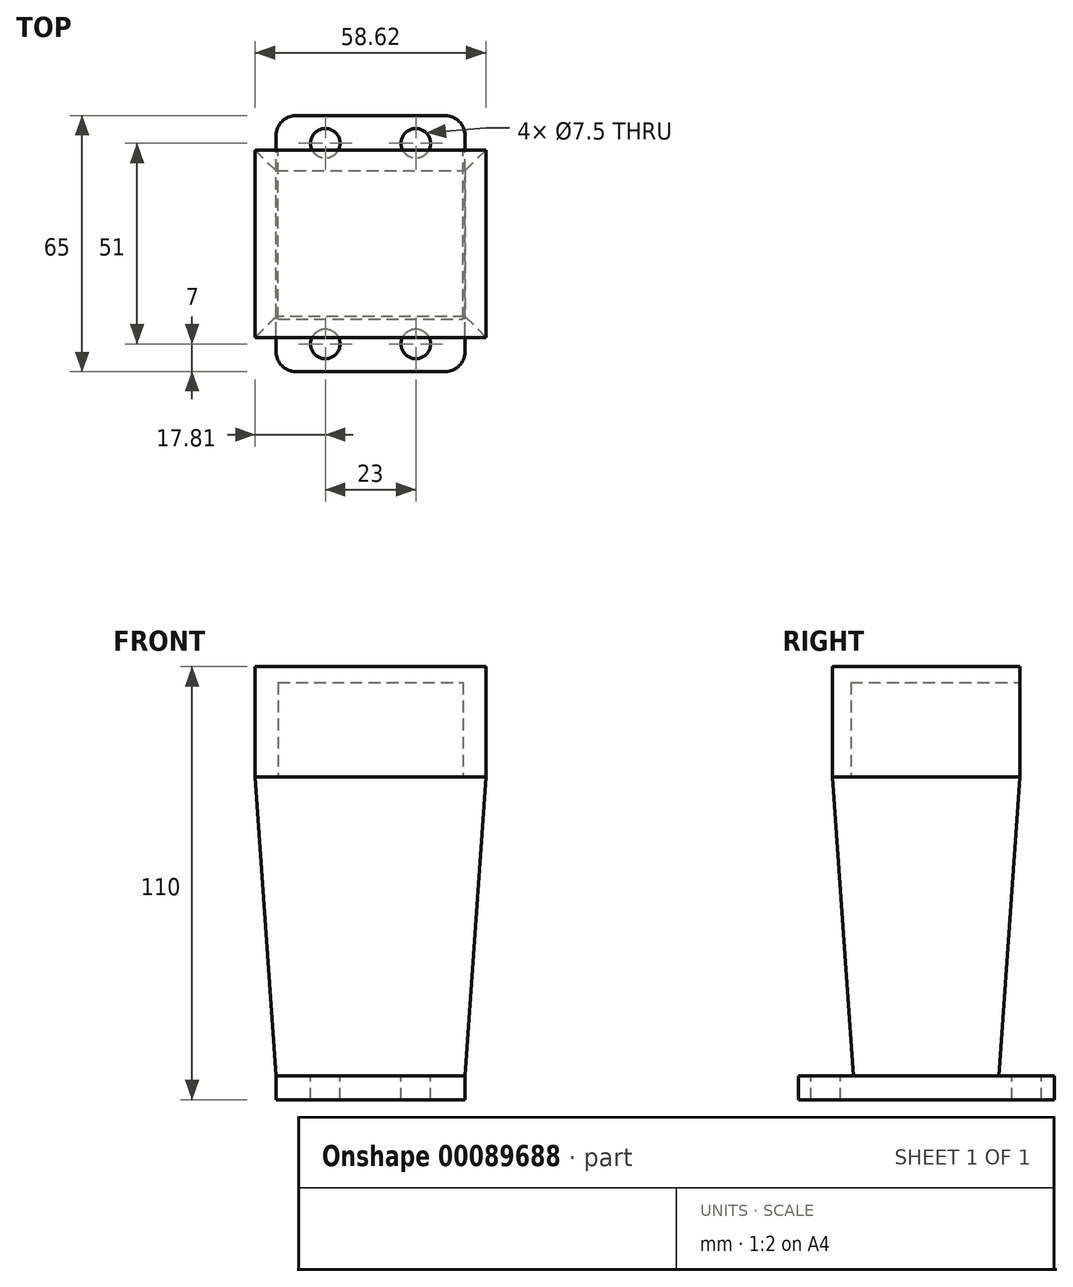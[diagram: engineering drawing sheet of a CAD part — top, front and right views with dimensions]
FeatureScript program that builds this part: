
annotation { "Feature Type Name" : "Feature", "Feature Type Description" : "" }
export const myFeature = defineFeature(function(context is Context, id is Id, definition is map)
    precondition{}
    {
        {
            var Q0;
            Q0=qCreatedBy(makeId("Top.planeOp"),FACE);
            var sketch = newSketch(context, id + "F0", { "sketchPlane" : qUnion([Q0])});
            skLineSegment(sketch, "E0.bottom", {"start": v(0, 0) * mm, "end": v(-48, 0) * mm});
            skLineSegment(sketch, "E0.top", {"start": v(0, 65) * mm, "end": v(-48, 65) * mm});
            skLineSegment(sketch, "E0.left", {"start": v(0, 0) * mm, "end": v(0, 65) * mm});
            skLineSegment(sketch, "E0.right", {"start": v(-48, 0) * mm, "end": v(-48, 65) * mm});
            skSolve(sketch);
        }
        {
            var Q0;
            Q0=makeQuery(id+"F0.imprint","IMPRINT",FACE,{"disambiguationData":[TD([[makeQuery(id+"F0.imprint","IMPRINT",EDGE,{"derivedFrom":sQuery(id+"F0.wireOp",EDGE,"E0.bottom")}),-1.0]])]});
            extrude(context, id + "F1", {"entities" : qUnion([Q0]), "depth" : 6 * mm});
        }
        {
            var Q0;
            Q0=makeQuery(id+"F1.opExtrude","CAP_FACE",FACE,{"disambiguationData":[OSD([sQuery(id+"F0.wireOp",EDGE,"E0.bottom"),sQuery(id+"F0.wireOp",EDGE,"E0.top"),sQuery(id+"F0.wireOp",EDGE,"E0.left"),sQuery(id+"F0.wireOp",EDGE,"E0.right")])],"isStart":false});
            var sketch = newSketch(context, id + "F2", { "sketchPlane" : qUnion([Q0])});
            skLineSegment(sketch, "E1", {"start": v(-24, 65) * mm, "end": v(-24, 0) * mm});
            skLineSegment(sketch, "E2", {"start": v(-48, 32.5) * mm, "end": v(0, 32.5) * mm});
            skLineSegment(sketch, "E3.bottom", {"start": v(0, 14) * mm, "end": v(-48, 14) * mm});
            skLineSegment(sketch, "E3.top", {"start": v(0, 51) * mm, "end": v(-48, 51) * mm});
            skLineSegment(sketch, "E3.left", {"start": v(0, 14) * mm, "end": v(0, 51) * mm});
            skLineSegment(sketch, "E3.right", {"start": v(-48, 14) * mm, "end": v(-48, 51) * mm});
            skPoint(sketch, "E3.middle", {"position": v(-24, 32.5) * mm});
            skSolve(sketch);
        }
        {
            var Q0;
            {var subQ0=sQuery(id+"F2.wireOp",EDGE,"E3.top");var subQ1=sQuery(id+"F2.wireOp",EDGE,"E1");var subQ2=makeQuery(id+"F2.imprint","INTERSECT",VERTEX,{"derivedFrom":[subQ1,subQ0]});Q0=makeQuery(id+"F2.imprint","IMPRINT",FACE,{"disambiguationData":[TD([[makeQuery(id+"F2.imprint","IMPRINT",EDGE,{"disambiguationData":[TD([[subQ2,-1.0]])],"derivedFrom":subQ1}),1.0]])]});}
            var Q1;
            {var subQ0=sQuery(id+"F2.wireOp",EDGE,"E3.top");var subQ1=sQuery(id+"F2.wireOp",EDGE,"E1");var subQ2=makeQuery(id+"F2.imprint","INTERSECT",VERTEX,{"derivedFrom":[subQ1,subQ0]});Q1=makeQuery(id+"F2.imprint","IMPRINT",FACE,{"disambiguationData":[TD([[makeQuery(id+"F2.imprint","IMPRINT",EDGE,{"disambiguationData":[TD([[subQ2,-1.0]])],"derivedFrom":subQ1}),-1.0]])]});}
            var Q2;
            {var subQ0=sQuery(id+"F2.wireOp",EDGE,"E2");var subQ1=sQuery(id+"F2.wireOp",EDGE,"E1");var subQ2=makeQuery(id+"F2.imprint","INTERSECT",VERTEX,{"derivedFrom":[subQ1,subQ0]});Q2=makeQuery(id+"F2.imprint","IMPRINT",FACE,{"disambiguationData":[TD([[makeQuery(id+"F2.imprint","IMPRINT",EDGE,{"disambiguationData":[TD([[subQ2,-1.0]])],"derivedFrom":subQ1}),-1.0]])]});}
            var Q3;
            {var subQ0=sQuery(id+"F2.wireOp",EDGE,"E2");var subQ1=sQuery(id+"F2.wireOp",EDGE,"E1");var subQ2=makeQuery(id+"F2.imprint","INTERSECT",VERTEX,{"derivedFrom":[subQ1,subQ0]});Q3=makeQuery(id+"F2.imprint","IMPRINT",FACE,{"disambiguationData":[TD([[makeQuery(id+"F2.imprint","IMPRINT",EDGE,{"disambiguationData":[TD([[subQ2,-1.0]])],"derivedFrom":subQ1}),1.0]])]});}
            extrude(context, id + "F3", {"entities" : qUnion([Q0, Q1, Q2, Q3]), "operationType" : NewBodyOperationType.ADD, "depth" : 76 * mm, "hasDraft" : true, "draftAngle" : 4 * degree});
        }
        {
            var Q0;
            Q0=makeQuery(id+"F3.opExtrude","CAP_FACE",FACE,{"disambiguationData":[OSD([sQuery(id+"F2.wireOp",EDGE,"E3.bottom"),sQuery(id+"F2.wireOp",EDGE,"E3.top"),sQuery(id+"F2.wireOp",EDGE,"E3.left"),sQuery(id+"F2.wireOp",EDGE,"E3.right")])],"isStart":false});
            extrude(context, id + "F4", {"entities" : qUnion([Q0]), "operationType" : NewBodyOperationType.ADD, "depth" : 28 * mm});
        }
        {
            var Q0;
            Q0=makeQuery(id+"F4.opExtrude","SWEPT_FACE",FACE,{"disambiguationData":[OSD([sQuery(id+"F2.wireOp",EDGE,"E3.top")])]});
            var sketch = newSketch(context, id + "F5", { "sketchPlane" : qUnion([Q0])});
            skLineSegment(sketch, "E4.bottom", {"start": v(47.5, 106) * mm, "end": v(0.5, 106) * mm});
            skLineSegment(sketch, "E4.top", {"start": v(47.5, 82) * mm, "end": v(0.5, 82) * mm});
            skLineSegment(sketch, "E4.left", {"start": v(47.5, 106) * mm, "end": v(47.5, 82) * mm});
            skLineSegment(sketch, "E4.right", {"start": v(0.5, 106) * mm, "end": v(0.5, 82) * mm});
            skPoint(sketch, "E4.middle", {"position": v(24, 94) * mm});
            skPoint(sketch, "E4.middle.positionSnap0", {"position": v(24, 110) * mm});
            skPoint(sketch, "E4.centerSnap0", {"position": v(24, 110) * mm});
            skSolve(sketch);
        }
        {
            var Q0;
            Q0=makeQuery(id+"F5.imprint","IMPRINT",FACE,{"disambiguationData":[TD([[makeQuery(id+"F5.imprint","IMPRINT",EDGE,{"derivedFrom":sQuery(id+"F5.wireOp",EDGE,"E4.bottom")}),1.0]])]});
            extrude(context, id + "F6", {"entities" : qUnion([Q0]), "operationType" : NewBodyOperationType.REMOVE, "oppositeDirection" : true, "depth" : 43 * mm});
        }
        {
            var Q0;
            {var subQ0=sQuery(id+"F0.wireOp",EDGE,"E0.right");var subQ1=sQuery(id+"F0.wireOp",EDGE,"E0.left");var subQ2=sQuery(id+"F0.wireOp",EDGE,"E0.top");Q0=makeQuery(id+"F3.boolean.opBoolean","SPLIT",FACE,{"disambiguationData":[TD([makeQuery(id+"F1.opExtrude","SWEPT_FACE",FACE,{"disambiguationData":[OSD([subQ2])]})])],"derivedFrom":makeQuery(id+"F1.opExtrude","CAP_FACE",FACE,{"disambiguationData":[OSD([sQuery(id+"F0.wireOp",EDGE,"E0.bottom"),subQ2,subQ1,subQ0])],"isStart":false})});}
            var sketch = newSketch(context, id + "F7", { "sketchPlane" : qUnion([Q0])});
            skCircle(sketch, "E5", {"center": v(-35.5, 58) * mm, "radius": 3.75 * mm});
            skCircle(sketch, "E6", {"center": v(-12.5, 58) * mm, "radius": 3.75 * mm});
            skSolve(sketch);
        }
        {
            var Q0;
            {var subQ0=sQuery(id+"F0.wireOp",EDGE,"E0.right");var subQ1=sQuery(id+"F0.wireOp",EDGE,"E0.left");var subQ2=sQuery(id+"F0.wireOp",EDGE,"E0.bottom");Q0=makeQuery(id+"F3.boolean.opBoolean","SPLIT",FACE,{"disambiguationData":[TD([makeQuery(id+"F1.opExtrude","SWEPT_FACE",FACE,{"disambiguationData":[OSD([subQ2])]})])],"derivedFrom":makeQuery(id+"F1.opExtrude","CAP_FACE",FACE,{"disambiguationData":[OSD([subQ2,sQuery(id+"F0.wireOp",EDGE,"E0.top"),subQ1,subQ0])],"isStart":false})});}
            var sketch = newSketch(context, id + "F8", { "sketchPlane" : qUnion([Q0])});
            skCircle(sketch, "E7", {"center": v(-35.5, 7) * mm, "radius": 3.75 * mm});
            skCircle(sketch, "E8", {"center": v(-12.5, 7) * mm, "radius": 3.75 * mm});
            skSolve(sketch);
        }
        {
            var Q0;
            Q0=makeQuery(id+"F8.imprint","IMPRINT",FACE,{"disambiguationData":[TD([[makeQuery(id+"F8.imprint","IMPRINT",EDGE,{"derivedFrom":sQuery(id+"F8.wireOp",EDGE,"E7")}),1.0]])]});
            var Q1;
            Q1=makeQuery(id+"F8.imprint","IMPRINT",FACE,{"disambiguationData":[TD([[makeQuery(id+"F8.imprint","IMPRINT",EDGE,{"derivedFrom":sQuery(id+"F8.wireOp",EDGE,"E8")}),1.0]])]});
            var Q2;
            Q2=makeQuery(id+"F7.imprint","IMPRINT",FACE,{"disambiguationData":[TD([[makeQuery(id+"F7.imprint","IMPRINT",EDGE,{"derivedFrom":sQuery(id+"F7.wireOp",EDGE,"E6")}),1.0]])]});
            var Q3;
            Q3=makeQuery(id+"F7.imprint","IMPRINT",FACE,{"disambiguationData":[TD([[makeQuery(id+"F7.imprint","IMPRINT",EDGE,{"derivedFrom":sQuery(id+"F7.wireOp",EDGE,"E5")}),1.0]])]});
            extrude(context, id + "F9", {"entities" : qUnion([Q0, Q1, Q2, Q3]), "operationType" : NewBodyOperationType.REMOVE, "oppositeDirection" : true, "depth" : 25 * mm});
        }
        {
            var Q0;
            Q0=makeQuery(id+"F1.opExtrude","SWEPT_EDGE",EDGE,{"disambiguationData":[OSD([sQuery(id+"F0.wireOp",EDGE,"E0.bottom"),sQuery(id+"F0.wireOp",EDGE,"E0.right")])]});
            var Q1;
            Q1=makeQuery(id+"F1.opExtrude","SWEPT_EDGE",EDGE,{"disambiguationData":[OSD([sQuery(id+"F0.wireOp",EDGE,"E0.bottom"),sQuery(id+"F0.wireOp",EDGE,"E0.left")])]});
            var Q2;
            Q2=makeQuery(id+"F1.opExtrude","SWEPT_EDGE",EDGE,{"disambiguationData":[OSD([sQuery(id+"F0.wireOp",EDGE,"E0.top"),sQuery(id+"F0.wireOp",EDGE,"E0.left")])]});
            var Q3;
            Q3=makeQuery(id+"F1.opExtrude","SWEPT_EDGE",EDGE,{"disambiguationData":[OSD([sQuery(id+"F0.wireOp",EDGE,"E0.top"),sQuery(id+"F0.wireOp",EDGE,"E0.right")])]});
            fillet(context, id + "F10", {"entities" : qUnion([Q0, Q1, Q2, Q3]), "radius" : 5 * mm, "tangentPropagation" : true, "allowEdgeOverflow" : false});
        }
    });
